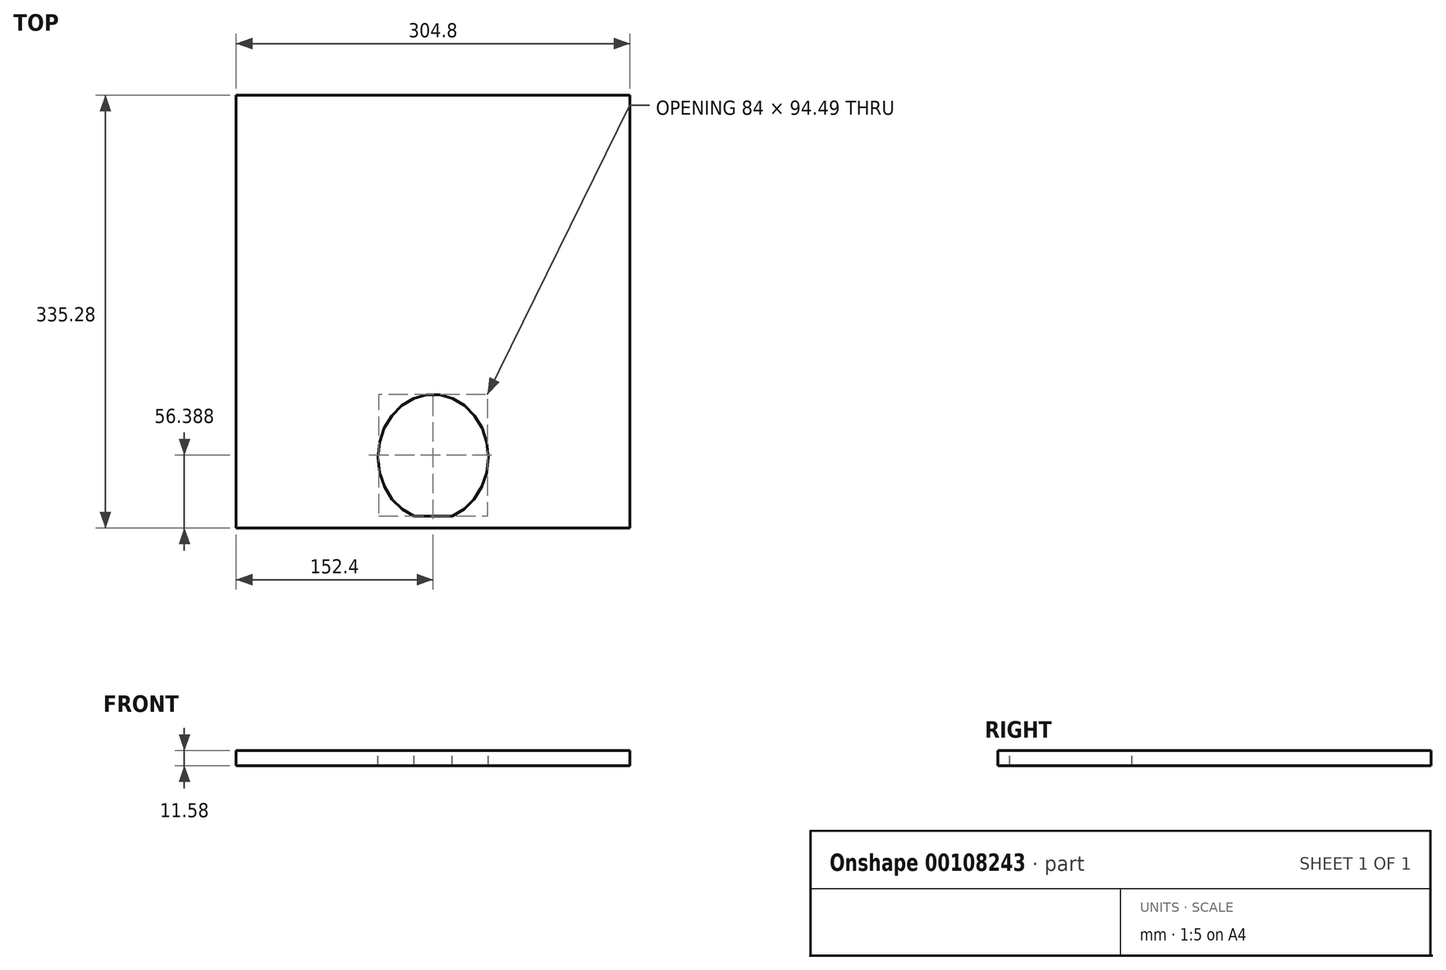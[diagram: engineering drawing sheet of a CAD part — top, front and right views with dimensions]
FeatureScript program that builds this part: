
annotation { "Feature Type Name" : "Feature", "Feature Type Description" : "" }
export const myFeature = defineFeature(function(context is Context, id is Id, definition is map)
    precondition{}
    {
        {
            var Q0;
            Q0=qCreatedBy(makeId("Top.planeOp"),FACE);
            var sketch = newSketch(context, id + "F0", { "sketchPlane" : qUnion([Q0])});
            skPoint(sketch, "E0.middle", {"position": v(0, 0) * mm});
            skLineSegment(sketch, "E1.bottom", {"start": v(-152.4, 167.64) * mm, "end": v(152.4, 167.64) * mm});
            skLineSegment(sketch, "E1.top", {"start": v(-152.4, -167.64) * mm, "end": v(152.4, -167.64) * mm});
            skLineSegment(sketch, "E1.left", {"start": v(-152.4, 167.64) * mm, "end": v(-152.4, -167.64) * mm});
            skLineSegment(sketch, "E1.right", {"start": v(152.4, 167.64) * mm, "end": v(152.4, -167.64) * mm});
            skPoint(sketch, "E2", {"position": v(0, 167.64) * mm});
            skPoint(sketch, "E3", {"position": v(152.4, 0) * mm});
            skSolve(sketch);
        }
        {
            var Q0;
            Q0=makeQuery(id+"F0.imprint","IMPRINT",FACE,{"disambiguationData":[TD([[makeQuery(id+"F0.imprint","IMPRINT",EDGE,{"derivedFrom":sQuery(id+"F0.wireOp",EDGE,"E1.bottom")}),-1.0]])]});
            extrude(context, id + "F1", {"entities" : qUnion([Q0]), "depth" : 11.58 * mm});
        }
        {
            var Q0;
            Q0=makeQuery(id+"F1.opExtrude","CAP_FACE",FACE,{"disambiguationData":[OSD([sQuery(id+"F0.wireOp",EDGE,"E1.bottom"),sQuery(id+"F0.wireOp",EDGE,"E1.top"),sQuery(id+"F0.wireOp",EDGE,"E1.left"),sQuery(id+"F0.wireOp",EDGE,"E1.right")])],"isStart":false});
            var sketch = newSketch(context, id + "F2", { "sketchPlane" : qUnion([Q0])});
            skEllipticalArc(sketch, "E4", {});
            skLineSegment(sketch, "E5", {"start": v(14.85, -158.5) * mm, "end": v(-14.85, -158.5) * mm});
            skPoint(sketch, "E6", {"position": v(0, -161.54) * mm});
            const initialGuessF2  = {"E4": [0, -0.112776, 0, 1, 0.048768, 0.042672, 3.4970138552800156, 2.786171451899571]};
            skSetInitialGuess(sketch, initialGuessF2);
            skSolve(sketch);
        }
        {
            var Q0;
            {var subQ0=sQuery(id+"F2.wireOp",EDGE,"E4");var subQ1=makeQuery(id+"F1.opExtrude","CAP_EDGE",EDGE,{"disambiguationData":[OSD([sQuery(id+"F0.wireOp",EDGE,"E1.top")])],"isStart":false});var subQ2=makeQuery(id+"F2.imprint","INTERSECT",VERTEX,{"disambiguationData":[OD(0.0)],"derivedFrom":[subQ1,subQ0]});Q0=makeQuery(id+"F2.imprint","IMPRINT",FACE,{"disambiguationData":[TD([[makeQuery(id+"F2.imprint","IMPRINT",EDGE,{"disambiguationData":[TD([[subQ2,1.0]])],"derivedFrom":subQ0}),1.0]])]});}
            extrude(context, id + "F3", {"entities" : qUnion([Q0]), "operationType" : NewBodyOperationType.REMOVE, "endBound" : BoundingType.THROUGH_ALL, "oppositeDirection" : true, "depth" : 30.48 * mm});
        }
    });
